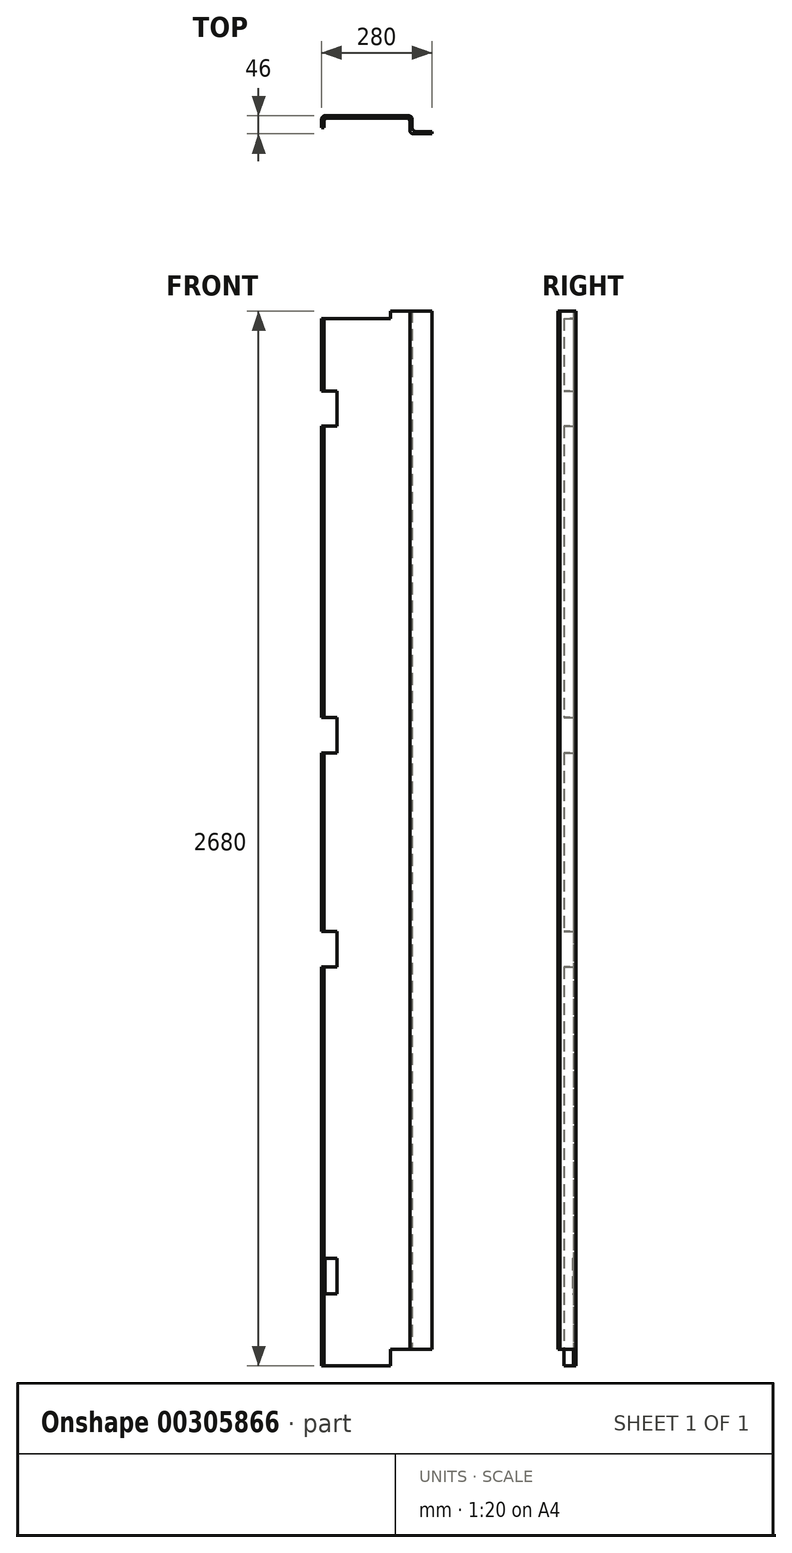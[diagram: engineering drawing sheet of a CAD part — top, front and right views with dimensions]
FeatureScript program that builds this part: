
annotation { "Feature Type Name" : "Feature", "Feature Type Description" : "" }
export const myFeature = defineFeature(function(context is Context, id is Id, definition is map)
    precondition{}
    {
        {
            var Q0;
            Q0=qCreatedBy(makeId("Top.planeOp"),FACE);
            var sketch = newSketch(context, id + "F0", { "sketchPlane" : qUnion([Q0])});
            skLineSegment(sketch, "E0", {"start": v(-127.67, 0) * mm, "end": v(-121.67, 0) * mm});
            skLineSegment(sketch, "E1", {"start": v(-127.67, 0) * mm, "end": v(-127.67, 21) * mm});
            skLineSegment(sketch, "E2", {"start": v(-118.67, 30) * mm, "end": v(93.33, 30) * mm});
            skLineSegment(sketch, "E3", {"start": v(102.33, 21) * mm, "end": v(102.33, -1) * mm});
            skLineSegment(sketch, "E4", {"start": v(111.33, -10) * mm, "end": v(152.33, -10) * mm});
            skLineSegment(sketch, "E5", {"start": v(152.33, -10) * mm, "end": v(152.33, -16) * mm});
            skLineSegment(sketch, "E6", {"start": v(-12.67, 30) * mm, "end": v(-12.67, 24) * mm});
            skPoint(sketch, "E6.endSnap0", {"position": v(-12.67, 30) * mm});
            skLineSegment(sketch, "E7", {"start": v(-121.67, 0) * mm, "end": v(-121.67, 15) * mm});
            skLineSegment(sketch, "E8", {"start": v(-112.67, 24) * mm, "end": v(87.33, 24) * mm});
            skLineSegment(sketch, "E9", {"start": v(96.33, 15) * mm, "end": v(96.33, -7) * mm});
            skLineSegment(sketch, "E10", {"start": v(105.33, -16) * mm, "end": v(152.33, -16) * mm});
            skPoint(sketch, "E11.visualSharp", {"position": v(-121.67, 24) * mm});
            skArc(sketch, "E11.filletArc", {"start": v(-112.67, 24) * mm, "mid": v(-119.03, 21.36) * mm, "end": v(-121.67, 15) * mm});
            skPoint(sketch, "E12.visualSharp", {"position": v(-127.67, 30) * mm});
            skArc(sketch, "E12.filletArc", {"start": v(-118.67, 30) * mm, "mid": v(-125.03, 27.36) * mm, "end": v(-127.67, 21) * mm});
            skPoint(sketch, "E13.visualSharp", {"position": v(102.33, 30) * mm});
            skArc(sketch, "E13.filletArc", {"start": v(102.33, 21) * mm, "mid": v(99.7, 27.36) * mm, "end": v(93.33, 30) * mm});
            skPoint(sketch, "E14.visualSharp", {"position": v(96.33, 24) * mm});
            skArc(sketch, "E14.filletArc", {"start": v(96.33, 15) * mm, "mid": v(93.7, 21.36) * mm, "end": v(87.33, 24) * mm});
            skPoint(sketch, "E15.visualSharp", {"position": v(96.33, -16) * mm});
            skArc(sketch, "E15.filletArc", {"start": v(96.33, -7) * mm, "mid": v(98.97, -13.36) * mm, "end": v(105.33, -16) * mm});
            skPoint(sketch, "E16.visualSharp", {"position": v(102.33, -10) * mm});
            skArc(sketch, "E16.filletArc", {"start": v(102.33, -1) * mm, "mid": v(104.97, -7.36) * mm, "end": v(111.33, -10) * mm});
            skSolve(sketch);
        }
        {
            var Q0;
            Q0 = qSketchRegion(id + "F0", true);
            extrude(context, id + "F1", {"entities" : qUnion([Q0]), "depth" : 2700 * mm});
        }
        {
            var Q0;
            Q0=makeQuery(id+"F1.opExtrude","SWEPT_FACE",FACE,{"disambiguationData":[OSD([sQuery(id+"F0.wireOp",EDGE,"E2")])]});
            var sketch = newSketch(context, id + "F2", { "sketchPlane" : qUnion([Q0])});
            skLineSegment(sketch, "E17.0", {"start": v(118.67, 0) * mm, "end": v(-93.33, 0) * mm});
            skLineSegment(sketch, "E18.0", {"start": v(127.67, 2700) * mm, "end": v(127.67, 0) * mm});
            skLineSegment(sketch, "E19.bottom", {"start": v(127.67, 0) * mm, "end": v(-47.33, 0) * mm});
            skLineSegment(sketch, "E19.top", {"start": v(127.67, 20) * mm, "end": v(-47.33, 20) * mm});
            skLineSegment(sketch, "E19.left", {"start": v(127.67, 0) * mm, "end": v(127.67, 20) * mm});
            skLineSegment(sketch, "E19.right", {"start": v(-47.33, 0) * mm, "end": v(-47.33, 20) * mm});
            skLineSegment(sketch, "E20", {"start": v(127.67, 1350) * mm, "end": v(0, 1350) * mm});
            skLineSegment(sketch, "E21.MirrorCS", {"start": v(127.67, 2680) * mm, "end": v(-47.33, 2680) * mm});
            skLineSegment(sketch, "E22.MirrorCS", {"start": v(-47.33, 2700) * mm, "end": v(-47.33, 2680) * mm});
            skLineSegment(sketch, "E23.MirrorCS", {"start": v(127.67, 2700) * mm, "end": v(-47.33, 2700) * mm});
            skLineSegment(sketch, "E24.MirrorCS", {"start": v(127.67, 2700) * mm, "end": v(127.67, 2680) * mm});
            skSolve(sketch);
        }
        {
            var Q0;
            Q0 = qSketchRegion(id + "F2", true);
            extrude(context, id + "F3", {"entities" : qUnion([Q0]), "operationType" : NewBodyOperationType.REMOVE, "endBound" : BoundingType.THROUGH_ALL, "oppositeDirection" : true, "depth" : 25 * mm});
        }
        {
            var Q0;
            Q0=makeQuery(id+"F1.opExtrude","SWEPT_FACE",FACE,{"disambiguationData":[OSD([sQuery(id+"F0.wireOp",EDGE,"E2")])]});
            var sketch = newSketch(context, id + "F4", { "sketchPlane" : qUnion([Q0])});
            skLineSegment(sketch, "E25.0", {"start": v(118.67, 20) * mm, "end": v(-47.33, 20) * mm});
            skLineSegment(sketch, "E26.0", {"start": v(118.67, 2680) * mm, "end": v(-47.33, 2680) * mm});
            skLineSegment(sketch, "E27.0", {"start": v(118.67, 2680) * mm, "end": v(118.67, 20) * mm});
            skLineSegment(sketch, "E28", {"start": v(-259.61, 1350) * mm, "end": v(-259.61, 2407) * mm});
            skPoint(sketch, "E28.startSnap0", {"position": v(-93.33, 1350) * mm});
            skLineSegment(sketch, "E29", {"start": v(-259.61, 2680) * mm, "end": v(-259.61, 2497) * mm});
            skLineSegment(sketch, "E30", {"start": v(-259.61, 2497) * mm, "end": v(-259.61, 2407) * mm});
            skLineSegment(sketch, "E31", {"start": v(-259.61, 2407) * mm, "end": v(-259.61, 1622) * mm});
            skLineSegment(sketch, "E32", {"start": v(-259.61, 1350) * mm, "end": v(-93.33, 1350) * mm});
            skLineSegment(sketch, "E33", {"start": v(-259.61, 1622) * mm, "end": v(-259.61, 1667) * mm});
            skLineSegment(sketch, "E34", {"start": v(-259.61, 1622) * mm, "end": v(-259.61, 1577) * mm});
            skLineSegment(sketch, "E35.MirrorCS", {"start": v(-259.61, 20) * mm, "end": v(-259.61, 203) * mm});
            skLineSegment(sketch, "E36.MirrorCS", {"start": v(-259.61, 293) * mm, "end": v(-259.61, 1078) * mm});
            skLineSegment(sketch, "E37.MirrorCS", {"start": v(-259.61, 1078) * mm, "end": v(-259.61, 1123) * mm});
            skLineSegment(sketch, "E38.MirrorCS", {"start": v(-259.61, 1350) * mm, "end": v(-259.61, 293) * mm});
            skLineSegment(sketch, "E39.MirrorCS", {"start": v(-259.61, 203) * mm, "end": v(-259.61, 293) * mm});
            skLineSegment(sketch, "E40.MirrorCS", {"start": v(-259.61, 1078) * mm, "end": v(-259.61, 1033) * mm});
            skLineSegment(sketch, "E41", {"start": v(-259.61, 2497) * mm, "end": v(118.67, 2497) * mm});
            skLineSegment(sketch, "E42", {"start": v(-259.61, 2407) * mm, "end": v(118.67, 2407) * mm});
            skLineSegment(sketch, "E43", {"start": v(-259.61, 1667) * mm, "end": v(118.67, 1667) * mm});
            skLineSegment(sketch, "E44", {"start": v(-259.61, 1577) * mm, "end": v(118.67, 1577) * mm});
            skLineSegment(sketch, "E45", {"start": v(-259.61, 1123) * mm, "end": v(118.67, 1123) * mm});
            skLineSegment(sketch, "E46", {"start": v(-259.61, 1033) * mm, "end": v(118.67, 1033) * mm});
            skLineSegment(sketch, "E47", {"start": v(-259.61, 293) * mm, "end": v(118.67, 293) * mm});
            skLineSegment(sketch, "E48", {"start": v(-259.61, 203) * mm, "end": v(118.67, 203) * mm});
            skLineSegment(sketch, "E49.0", {"start": v(127.67, 2680) * mm, "end": v(127.67, 20) * mm});
            skLineSegment(sketch, "E50", {"start": v(127.67, 2497) * mm, "end": v(89.1, 2497) * mm});
            skLineSegment(sketch, "E51", {"start": v(89.1, 2497) * mm, "end": v(89.1, 2407) * mm});
            skLineSegment(sketch, "E52", {"start": v(89.1, 2407) * mm, "end": v(127.67, 2407) * mm});
            skLineSegment(sketch, "E53", {"start": v(89.1, 1667) * mm, "end": v(89.1, 1577) * mm});
            skLineSegment(sketch, "E54", {"start": v(89.1, 1577) * mm, "end": v(127.67, 1577) * mm});
            skLineSegment(sketch, "E55", {"start": v(89.1, 1667) * mm, "end": v(127.67, 1667) * mm});
            skLineSegment(sketch, "E56", {"start": v(89.1, 1123) * mm, "end": v(127.67, 1123) * mm});
            skLineSegment(sketch, "E57", {"start": v(89.1, 1123) * mm, "end": v(89.1, 1033) * mm});
            skLineSegment(sketch, "E58", {"start": v(89.1, 1033) * mm, "end": v(127.67, 1033) * mm});
            skLineSegment(sketch, "E59", {"start": v(89.1, 293) * mm, "end": v(89.1, 203) * mm});
            skLineSegment(sketch, "E60", {"start": v(89.1, 203) * mm, "end": v(127.67, 203) * mm});
            skLineSegment(sketch, "E61", {"start": v(127.67, 203) * mm, "end": v(127.67, 293) * mm});
            skLineSegment(sketch, "E62", {"start": v(127.67, 293) * mm, "end": v(89.1, 293) * mm});
            skSolve(sketch);
        }
        {
            var Q0;
            {var subQ5=sQuery(id+"F4.wireOp",EDGE,"E51");Q0=makeQuery(id+"F4.imprint","IMPRINT",FACE,{"disambiguationData":[TD([[makeQuery(id+"F4.imprint","IMPRINT",EDGE,{"derivedFrom":subQ5}),1.0]])]});}
            var Q1;
            {var subQ0=sQuery(id+"F4.wireOp",EDGE,"E50");var subQ1=sQuery(id+"F4.wireOp",EDGE,"E27.0");var subQ2=makeQuery(id+"F4.imprint","INTERSECT",VERTEX,{"derivedFrom":[subQ1,subQ0]});Q1=makeQuery(id+"F4.imprint","IMPRINT",FACE,{"disambiguationData":[TD([[makeQuery(id+"F4.imprint","IMPRINT",EDGE,{"disambiguationData":[TD([[subQ2,-1.0]])],"derivedFrom":subQ1}),1.0]])]});}
            var Q2;
            {var subQ5=sQuery(id+"F4.wireOp",EDGE,"E61");Q2=makeQuery(id+"F4.imprint","IMPRINT",FACE,{"disambiguationData":[TD([[makeQuery(id+"F4.imprint","IMPRINT",EDGE,{"derivedFrom":subQ5}),1.0]])]});}
            var Q3;
            {var subQ5=sQuery(id+"F4.wireOp",EDGE,"E59");Q3=makeQuery(id+"F4.imprint","IMPRINT",FACE,{"disambiguationData":[TD([[makeQuery(id+"F4.imprint","IMPRINT",EDGE,{"derivedFrom":subQ5}),1.0]])]});}
            var Q4;
            {var subQ5=sQuery(id+"F4.wireOp",EDGE,"E57");Q4=makeQuery(id+"F4.imprint","IMPRINT",FACE,{"disambiguationData":[TD([[makeQuery(id+"F4.imprint","IMPRINT",EDGE,{"derivedFrom":subQ5}),1.0]])]});}
            var Q5;
            {var subQ0=sQuery(id+"F4.wireOp",EDGE,"E56");var subQ1=sQuery(id+"F4.wireOp",EDGE,"E27.0");var subQ2=makeQuery(id+"F4.imprint","INTERSECT",VERTEX,{"derivedFrom":[subQ1,subQ0]});Q5=makeQuery(id+"F4.imprint","IMPRINT",FACE,{"disambiguationData":[TD([[makeQuery(id+"F4.imprint","IMPRINT",EDGE,{"disambiguationData":[TD([[subQ2,-1.0]])],"derivedFrom":subQ1}),1.0]])]});}
            var Q6;
            {var subQ5=sQuery(id+"F4.wireOp",EDGE,"E53");Q6=makeQuery(id+"F4.imprint","IMPRINT",FACE,{"disambiguationData":[TD([[makeQuery(id+"F4.imprint","IMPRINT",EDGE,{"derivedFrom":subQ5}),1.0]])]});}
            var Q7;
            {var subQ0=sQuery(id+"F4.wireOp",EDGE,"E55");var subQ1=sQuery(id+"F4.wireOp",EDGE,"E27.0");var subQ2=makeQuery(id+"F4.imprint","INTERSECT",VERTEX,{"derivedFrom":[subQ1,subQ0]});Q7=makeQuery(id+"F4.imprint","IMPRINT",FACE,{"disambiguationData":[TD([[makeQuery(id+"F4.imprint","IMPRINT",EDGE,{"disambiguationData":[TD([[subQ2,-1.0]])],"derivedFrom":subQ1}),1.0]])]});}
            extrude(context, id + "F5", {"entities" : qUnion([Q0, Q1, Q2, Q3, Q4, Q5, Q6, Q7]), "operationType" : NewBodyOperationType.REMOVE, "endBound" : BoundingType.THROUGH_ALL, "oppositeDirection" : true, "depth" : 25 * mm});
        }
        {
            var Q0;
            Q0=makeQuery(id+"F1.opExtrude","SWEPT_FACE",FACE,{"disambiguationData":[OSD([sQuery(id+"F0.wireOp",EDGE,"E2")])]});
            var sketch = newSketch(context, id + "F6", { "sketchPlane" : qUnion([Q0])});
            skLineSegment(sketch, "E63.bottom", {"start": v(-47.33, 2700) * mm, "end": v(-167.33, 2700) * mm, "construction": true});
            skLineSegment(sketch, "E63.top", {"start": v(-47.33, 2638) * mm, "end": v(-167.33, 2638) * mm, "construction": true});
            skLineSegment(sketch, "E63.left", {"start": v(-47.33, 2700) * mm, "end": v(-47.33, 2638) * mm, "construction": true});
            skLineSegment(sketch, "E63.right", {"start": v(-167.33, 2700) * mm, "end": v(-167.33, 2638) * mm, "construction": true});
            skLineSegment(sketch, "E64", {"start": v(-93.33, 1350) * mm, "end": v(-309.38, 1350) * mm});
            skLineSegment(sketch, "E65.MirrorCS", {"start": v(-167.33, 0) * mm, "end": v(-167.33, 62) * mm});
            skLineSegment(sketch, "E66.MirrorCS", {"start": v(-47.33, 0) * mm, "end": v(-47.33, 62) * mm});
            skLineSegment(sketch, "E67.MirrorCS", {"start": v(-47.33, 62) * mm, "end": v(-167.33, 62) * mm});
            skLineSegment(sketch, "E68.MirrorCS", {"start": v(-47.33, 0) * mm, "end": v(-167.33, 0) * mm});
            skSolve(sketch);
        }
        {
            var Q0;
            Q0 = qSketchRegion(id + "F6", true);
            extrude(context, id + "F7", {"entities" : qUnion([Q0]), "operationType" : NewBodyOperationType.REMOVE, "endBound" : BoundingType.THROUGH_ALL, "oppositeDirection" : true, "depth" : 25 * mm});
        }
    });
